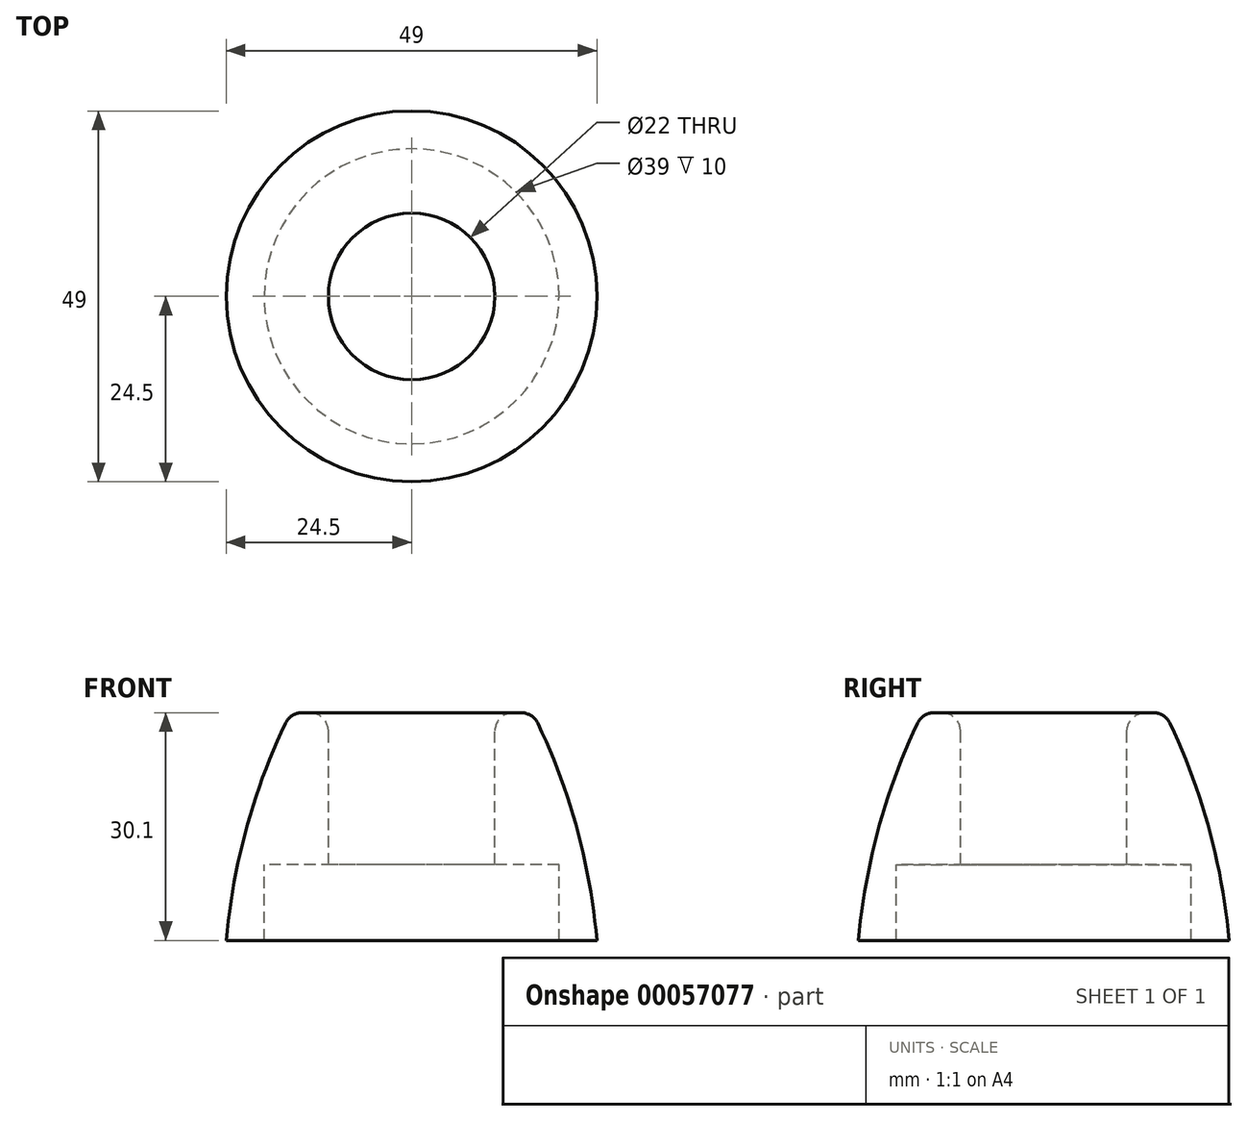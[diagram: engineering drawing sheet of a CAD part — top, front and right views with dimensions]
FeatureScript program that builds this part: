
annotation { "Feature Type Name" : "Feature", "Feature Type Description" : "" }
export const myFeature = defineFeature(function(context is Context, id is Id, definition is map)
    precondition{}
    {
        {
            var Q0;
            Q0=qCreatedBy(makeId("Right.planeOp"),FACE);
            var sketch = newSketch(context, id + "F0", { "sketchPlane" : qUnion([Q0])});
            skLineSegment(sketch, "E0", {"start": v(-11, 20) * mm, "end": v(-11, 0) * mm});
            skLineSegment(sketch, "E1", {"start": v(-11, 0) * mm, "end": v(0, 0) * mm});
            skLineSegment(sketch, "E2", {"start": v(0, 0) * mm, "end": v(0, -0.1) * mm});
            skLineSegment(sketch, "E3", {"start": v(0, -0.1) * mm, "end": v(-19.5, -0.1) * mm});
            skLineSegment(sketch, "E4", {"start": v(-19.5, -0.1) * mm, "end": v(-19.5, -10.1) * mm});
            skLineSegment(sketch, "E5", {"start": v(-19.5, -10.1) * mm, "end": v(-24.5, -10.1) * mm});
            skLineSegment(sketch, "E6", {"start": v(-11, 20) * mm, "end": v(-16, 20) * mm});
            skArc(sketch, "E7", {"start": v(-16, 20) * mm, "mid": v(-21.66, 5.35) * mm, "end": v(-24.5, -10.1) * mm});
            skLineSegment(sketch, "E8", {"start": v(-11, 0) * mm, "end": v(-11, -0.1) * mm});
            skSolve(sketch);
        }
        {
            var Q0;
            Q0=makeQuery(id+"F0.imprint","IMPRINT",FACE,{"disambiguationData":[TD([[makeQuery(id+"F0.imprint","IMPRINT",EDGE,{"derivedFrom":sQuery(id+"F0.wireOp",EDGE,"E0")}),-1.0]])]});
            var Q1;
            Q1=sQuery(id+"F0.wireOp",EDGE,"E2");
            revolve(context, id + "F1", {"entities" : qUnion([Q0]), "axis" : qUnion([Q1]), "revolveType" : RevolveType.FULL});
        }
        {
            var Q0;
            Q0=makeQuery(id+"F1.opRevolve","SWEPT_EDGE",EDGE,{"disambiguationData":[OSD([sQuery(id+"F0.wireOp",EDGE,"E0"),sQuery(id+"F0.wireOp",EDGE,"E6")])]});
            var Q1;
            Q1=makeQuery(id+"F1.opRevolve","SWEPT_EDGE",EDGE,{"disambiguationData":[OSD([sQuery(id+"F0.wireOp",EDGE,"E6"),sQuery(id+"F0.wireOp",EDGE,"E7")])]});
            fillet(context, id + "F2", {"entities" : qUnion([Q0, Q1]), "radius" : 2.5 * mm, "tangentPropagation" : true, "allowEdgeOverflow" : false});
        }
    });
